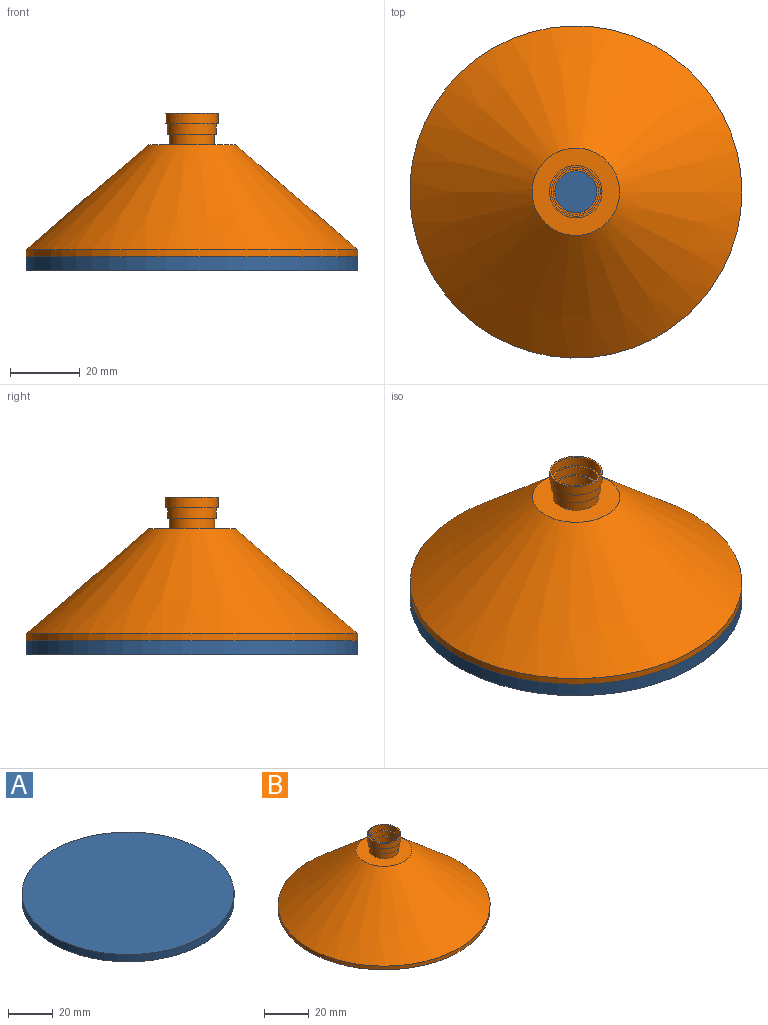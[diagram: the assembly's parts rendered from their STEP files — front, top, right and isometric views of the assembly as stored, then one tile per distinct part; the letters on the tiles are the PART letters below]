
ASSEMBLY  parts=2 mates=1
PART A: 3 faces, bbox 95x95x4 mm
  f0: cylinder r=47.5mm len=95mm, axis (0,0,1), area 1193.8mm2, adj f1,f2
  f1: plane 95x95mm, normal (0,0,-1), area 7088.2mm2, adj f0
  f2: plane 95x95mm, normal (0,0,1), area 7088.2mm2, adj f0
PART B: 18 faces, bbox 95x95x41 mm
  f0: cone r=12.5mm half-angle=49.4deg, axis (0,0,-1), area 8689.2mm2, adj f1,f15
  f1: plane 25x25mm, normal (0,0,1), area 358.1mm2, adj f0,f4
  f2: plane 23.52x23.52mm, normal (0,0,-1), area 321.4mm2, adj f3,f14
  f3: cone r=44.43mm half-angle=49.4deg, axis (0,0,-1), area 7594.5mm2, adj f2,f16
  f4: cylinder r=6.5mm len=13mm, axis (0,0,-1), area 122.5mm2, adj f1,f6
  f5: cylinder r=7mm len=14mm, axis (0,0,-1), area 131.9mm2, adj f6,f9
  f6: plane 14x14mm, normal (0,0,-1), area 21.2mm2, adj f4,f5
  f7: cylinder r=7.5mm len=15mm, axis (0,0,-1), area 141.4mm2, adj f8,f9
  f8: plane 15x15mm, normal (0,0,1), area 22.8mm2, adj f7,f10
  f9: plane 15x15mm, normal (0,0,-1), area 22.8mm2, adj f5,f7
  f10: cylinder r=7mm len=14mm, axis (0,0,1), area 127.5mm2, adj f8,f11
  f11: plane 14x14mm, normal (0,0,1), area 21.2mm2, adj f10,f12
  f12: cylinder r=6.5mm len=13mm, axis (0,0,1), area 118.4mm2, adj f11,f13
  f13: plane 13x13mm, normal (0,0,1), area 19.6mm2, adj f12,f14
  f14: cylinder r=6mm len=12mm, axis (0,0,1), area 196mm2, adj f2,f13
  f15: cylinder r=47.5mm len=95mm, axis (0,0,1), area 596.9mm2, adj f0,f17
  f16: cylinder r=44.43mm len=88.85mm, axis (0,0,1), area 558.3mm2, adj f3,f17
  f17: plane 95x95mm, normal (0,0,-1), area 887.5mm2, adj f15,f16
PLACE A t=(-59.8,-16.61,26.2)mm
PLACE B t=(-59.8,-16.61,26.2)mm
MATE fastened B.f0 <-> A.f0  axis (0,0,-1) through (-59.8,-16.61,24.2)mm
